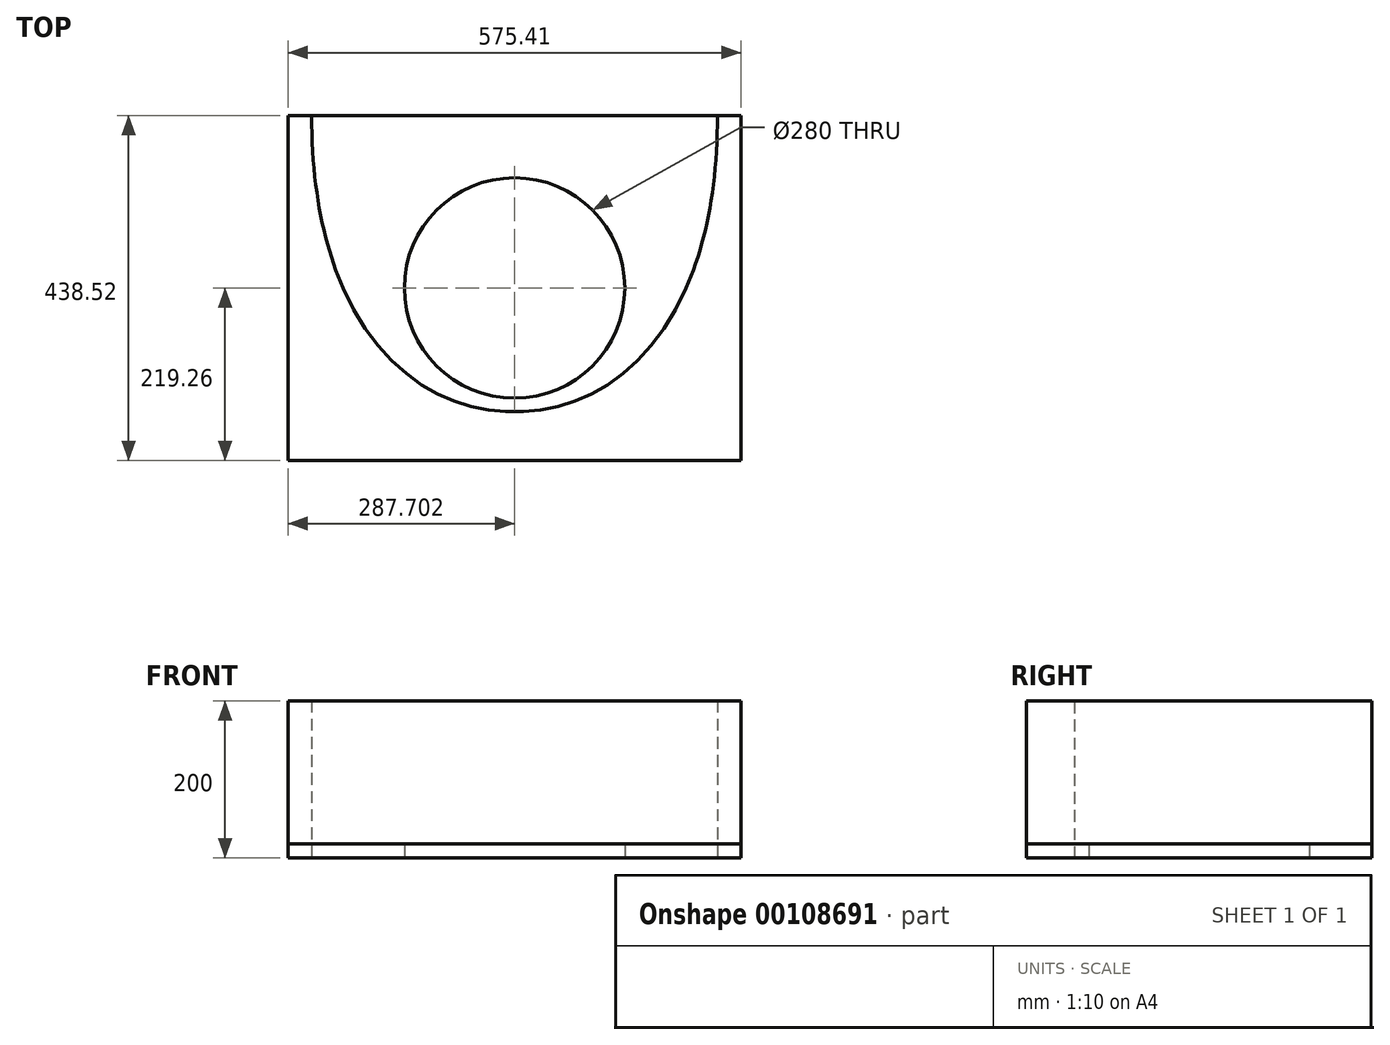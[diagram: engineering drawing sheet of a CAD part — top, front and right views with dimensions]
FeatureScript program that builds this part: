
annotation { "Feature Type Name" : "Feature", "Feature Type Description" : "" }
export const myFeature = defineFeature(function(context is Context, id is Id, definition is map)
    precondition{}
    {
        {
            var Q0;
            Q0=qCreatedBy(makeId("Top.planeOp"),FACE);
            var sketch = newSketch(context, id + "F0", { "sketchPlane" : qUnion([Q0])});
            skCircle(sketch, "E0", {"center": v(72.84, 0) * mm, "radius": 157.5 * mm, "construction": true});
            skFitSpline(sketch, "E1", {"points": [v(-184.86, 219.26) * mm, v(72.84, -157.5) * mm, v(330.55, 219.26) * mm], "startDerivative": vector(0, -1593.86) * mm, "endDerivative": vector(0, 1593.86) * mm});
            skLineSegment(sketch, "E2", {"start": v(72.84, 590.77) * mm, "end": v(72.84, -480.39) * mm, "construction": true});
            skLineSegment(sketch, "E3", {"start": v(-409.96, 219.26) * mm, "end": v(555.64, 219.26) * mm, "construction": true});
            skLineSegment(sketch, "E4", {"start": v(-184.86, 683.23) * mm, "end": v(-184.86, -475.85) * mm, "construction": true});
            skLineSegment(sketch, "E5", {"start": v(-409.96, 0) * mm, "end": v(555.64, 0) * mm, "construction": true});
            skLineSegment(sketch, "E6", {"start": v(-409.96, -219.26) * mm, "end": v(555.64, -219.26) * mm, "construction": true});
            skFitSpline(sketch, "E7", {"points": [v(-184.86, -219.26) * mm, v(72.84, 157.5) * mm, v(330.55, -219.26) * mm], "startDerivative": vector(0, 1593.86) * mm, "endDerivative": vector(0, -1593.86) * mm});
            skLineSegment(sketch, "E8", {"start": v(330.55, 219.26) * mm, "end": v(-184.86, 219.26) * mm});
            skLineSegment(sketch, "E9", {"start": v(-184.86, -219.26) * mm, "end": v(330.55, -219.26) * mm});
            skCircle(sketch, "E10", {"center": v(72.84, 0) * mm, "radius": 140 * mm});
            skLineSegment(sketch, "E11", {"start": v(-184.86, 219.26) * mm, "end": v(-214.86, 219.26) * mm});
            skLineSegment(sketch, "E12", {"start": v(-214.86, 219.26) * mm, "end": v(-214.86, -219.26) * mm});
            skLineSegment(sketch, "E13", {"start": v(-214.86, -219.26) * mm, "end": v(-184.86, -219.26) * mm});
            skLineSegment(sketch, "E14", {"start": v(330.55, 219.26) * mm, "end": v(360.55, 219.26) * mm});
            skLineSegment(sketch, "E15", {"start": v(360.55, 219.26) * mm, "end": v(360.55, -219.26) * mm});
            skLineSegment(sketch, "E16", {"start": v(360.55, -219.26) * mm, "end": v(330.55, -219.26) * mm});
            skSolve(sketch);
        }
        {
            var Q0;
            {var subQ4=sQuery(id+"F0.wireOp",EDGE,"E11");Q0=makeQuery(id+"F0.imprint","IMPRINT",FACE,{"disambiguationData":[TD([[makeQuery(id+"F0.imprint","IMPRINT",EDGE,{"derivedFrom":subQ4}),1.0]])]});}
            var Q1;
            {var subQ4=sQuery(id+"F0.wireOp",EDGE,"E9");Q1=makeQuery(id+"F0.imprint","IMPRINT",FACE,{"disambiguationData":[TD([[makeQuery(id+"F0.imprint","IMPRINT",EDGE,{"derivedFrom":subQ4}),1.0]])]});}
            var Q2;
            {var subQ0=sQuery(id+"F0.wireOp",EDGE,"E14");Q2=makeQuery(id+"F0.imprint","IMPRINT",FACE,{"disambiguationData":[TD([[makeQuery(id+"F0.imprint","IMPRINT",EDGE,{"derivedFrom":subQ0}),-1.0]])]});}
            extrude(context, id + "F1", {"entities" : qUnion([Q0, Q1, Q2]), "depth" : 200 * mm});
        }
        {
            var Q0;
            {var subQ4=sQuery(id+"F0.wireOp",EDGE,"E9");Q0=makeQuery(id+"F0.imprint","IMPRINT",FACE,{"disambiguationData":[TD([[makeQuery(id+"F0.imprint","IMPRINT",EDGE,{"derivedFrom":subQ4}),1.0]])]});}
            var Q1;
            {var subQ0=sQuery(id+"F0.wireOp",EDGE,"E14");Q1=makeQuery(id+"F0.imprint","IMPRINT",FACE,{"disambiguationData":[TD([[makeQuery(id+"F0.imprint","IMPRINT",EDGE,{"derivedFrom":subQ0}),-1.0]])]});}
            var Q2;
            {var subQ4=sQuery(id+"F0.wireOp",EDGE,"E11");Q2=makeQuery(id+"F0.imprint","IMPRINT",FACE,{"disambiguationData":[TD([[makeQuery(id+"F0.imprint","IMPRINT",EDGE,{"derivedFrom":subQ4}),1.0]])]});}
            var Q3;
            Q3=makeQuery(id+"F0.imprint","IMPRINT",FACE,{"disambiguationData":[TD([[makeQuery(id+"F0.imprint","IMPRINT",EDGE,{"derivedFrom":sQuery(id+"F0.wireOp",EDGE,"E10")}),-1.0]])]});
            var Q4;
            {var subQ0=sQuery(id+"F0.wireOp",EDGE,"E8");Q4=makeQuery(id+"F0.imprint","IMPRINT",FACE,{"disambiguationData":[TD([[makeQuery(id+"F0.imprint","IMPRINT",EDGE,{"derivedFrom":subQ0}),1.0]])]});}
            extrude(context, id + "F2", {"entities" : qUnion([Q0, Q1, Q2, Q3, Q4]), "depth" : 18 * mm});
        }
    });
